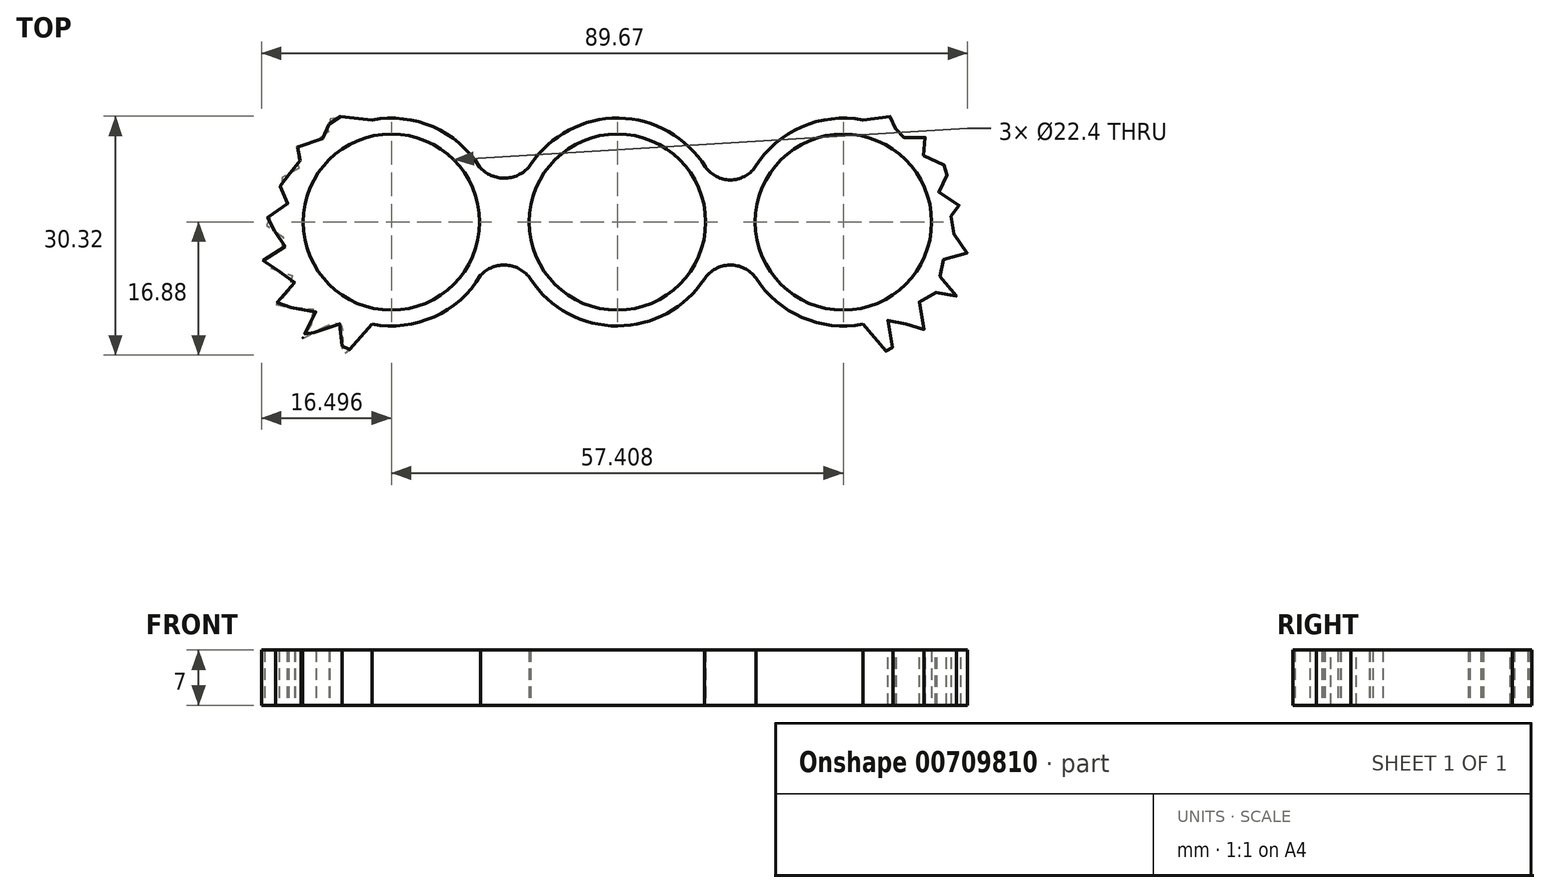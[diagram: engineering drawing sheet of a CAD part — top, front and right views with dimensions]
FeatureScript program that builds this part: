
annotation { "Feature Type Name" : "Feature", "Feature Type Description" : "" }
export const myFeature = defineFeature(function(context is Context, id is Id, definition is map)
    precondition{}
    {
        {
            var Q0;
            Q0=qCreatedBy(makeId("Top.planeOp"),FACE);
            var sketch = newSketch(context, id + "F0", { "sketchPlane" : qUnion([Q0])});
            skCircle(sketch, "E0", {"center": v(0, 0) * mm, "radius": 11.2 * mm});
            skCircle(sketch, "E1.1.0", {"center": v(28.7, 0) * mm, "radius": 11.2 * mm});
            skArc(sketch, "E2", {"start": v(-11.03, -7.25) * mm, "mid": v(0.03, -13.2) * mm, "end": v(11.06, -7.21) * mm});
            skArc(sketch, "E3", {"start": v(31.17, 12.97) * mm, "mid": v(23.41, 12.1) * mm, "end": v(17.5, 6.99) * mm});
            skArc(sketch, "E4.1.0", {"start": v(-31.17, -12.97) * mm, "mid": v(-23.29, -12.04) * mm, "end": v(-17.36, -6.75) * mm});
            skCircle(sketch, "E4.1.1", {"center": v(-28.7, 0) * mm, "radius": 11.2 * mm});
            skFitSpline(sketch, "E5", {"points": [v(-31.17, 12.97) * mm, v(-36.55, 12.97) * mm, v(-36.75, 11.03) * mm, v(-40.98, 9.22) * mm, v(-40.17, 7.2) * mm, v(-42.98, 5.2) * mm, v(-41.78, 2.58) * mm, v(-44.8, 0) * mm, v(-41.98, -2.64) * mm, v(-45.2, -5.25) * mm, v(-40.98, -7.26) * mm, v(-43.39, -10.68) * mm, v(-38.36, -11.28) * mm, v(-39.97, -14.7) * mm, v(-35.35, -12.9) * mm, v(-34.95, -16.51) * mm, v(-31.17, -12.97) * mm], "startDerivative": vector(-102.3, 16) * mm, "endDerivative": vector(72.61, 89.08) * mm});
            skFitSpline(sketch, "E6", {"points": [v(31.17, 12.97) * mm, v(35.4, 12.97) * mm, v(35.4, 10.82) * mm, v(39.02, 10.82) * mm, v(39.02, 8.21) * mm, v(42.44, 6.8) * mm, v(40.63, 4.2) * mm, v(43.64, 1.78) * mm, v(41.83, 0) * mm, v(44.45, -3.85) * mm, v(40.43, -5.46) * mm, v(43.04, -9.48) * mm, v(38.62, -9.07) * mm, v(38.82, -13.9) * mm, v(34.6, -12.09) * mm, v(35, -16.71) * mm, v(31.17, -12.97) * mm], "startDerivative": vector(91.15, 18.84) * mm, "endDerivative": vector(-75.39, 93.62) * mm});
            skArc(sketch, "E7", {"start": v(-18.08, 7.83) * mm, "mid": v(-14.7, 5.6) * mm, "end": v(-11, 7.29) * mm});
            skArc(sketch, "E8", {"start": v(11, 7.29) * mm, "mid": v(14.35, 5.36) * mm, "end": v(17.7, 7.29) * mm});
            skArc(sketch, "E9", {"start": v(-11, -7.29) * mm, "mid": v(-14.7, -5.46) * mm, "end": v(-18.08, -7.83) * mm});
            skArc(sketch, "E10", {"start": v(17.58, -7.1) * mm, "mid": v(14.24, -5.46) * mm, "end": v(11, -7.29) * mm});
            skArc(sketch, "E11.trimOffspring", {"start": v(-17.52, 7.02) * mm, "mid": v(-23.43, 12.1) * mm, "end": v(-31.17, 12.97) * mm});
            skArc(sketch, "E12.trimOffspring", {"start": v(17.58, -7.1) * mm, "mid": v(23.47, -12.12) * mm, "end": v(31.17, -12.97) * mm});
            skArc(sketch, "E13.trimOffspring", {"start": v(11.2, 6.99) * mm, "mid": v(0.18, 13.2) * mm, "end": v(-11, 7.29) * mm});
            skSolve(sketch);
        }
        {
            var Q0;
            Q0 = qSketchRegion(id + "F0", true);
            extrude(context, id + "F1", {"entities" : qUnion([Q0]), "depth" : 7 * mm, "offsetDistance" : 25 * mm});
        }
    });
